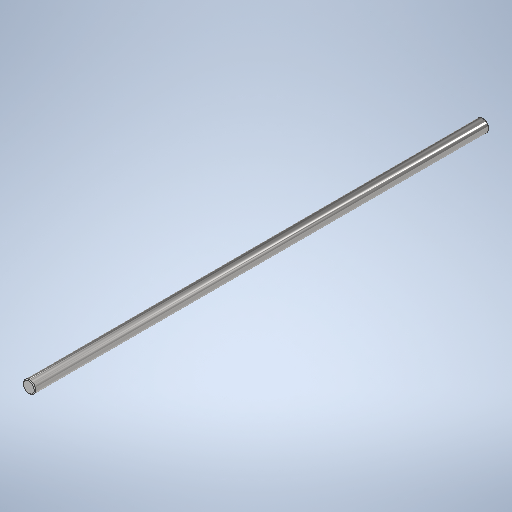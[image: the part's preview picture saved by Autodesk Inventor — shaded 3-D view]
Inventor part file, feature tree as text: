
AUTODESK INVENTOR PART (.ipt)
format: ipt  version: 2025.2 (Build 292293000, 293)  size: 259,072 bytes
history: native  units: mm
features: extrude x1, chamfer x1, sketch x1
ambient origin geometry x8: Origin, YZ Plane, XZ Plane, XY Plane, X Axis, Y Axis, Z Axis, Center Point
bodies: Solid1 (feature_tree)
feature tree (3):
  extrude  "Extrusion1"  Depth=297.0mm TaperAngle=0.0deg
  chamfer  "Chamfer1"  Distance=0.5mm Angle=45.0deg
  sketch  "Sketch1"  dims[d0=8.0mm d1=297.0mm d2=0.0mm d3=0.5mm d4=2.0mm d5=45.0deg]
